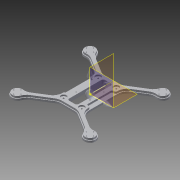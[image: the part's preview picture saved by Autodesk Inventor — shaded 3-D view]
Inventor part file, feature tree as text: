
AUTODESK INVENTOR PART (.ipt)
format: ipt  version: 2013 (Build 170138000, 138)  size: 2,560,512 bytes
history: native  units: mm
features: sketch x7, mirror x5, extrude x4, fillet x4, hole x4, projected_geometry x1
ambient origin geometry x8: Origin, YZ Plane, XZ Plane, XY Plane, X Axis, Y Axis, Z Axis, Center Point
feature tree (25):
  extrude  "Extrusion2"  Depth=80.0mm
  fillet  "Fillet1"  Radius=5.0mm
  fillet  "Fillet2"  Radius=5.0mm
  extrude  "Extrusion3"  Depth=30.0mm
  hole  "Hole1"  [1 undecoded]
  hole  "Hole2"  [1 undecoded]
  hole  "Hole3"  [1 undecoded]
  mirror  "Mirror1"
  mirror  "Mirror2"
  hole  "Hole4"  [1 undecoded]
  mirror  "Mirror3"
  mirror  "Mirror4"
  extrude  "Extrusion4"  Depth=20.0mm
  fillet  "Fillet3"  Radius=38.0mm
  extrude  "Extrusion5"  Depth=8.0mm
  mirror  "Mirror5"
  fillet  "Fillet5"  Radius=40.0mm
  sketch  "Sketch3"  dims[d13=80.0mm d14=80.0mm d15=5.0mm d16=5.0mm]
  sketch  "Sketch4"  dims[d17=25.0mm d18=30.0mm]
  sketch  "Sketch5"  dims[d19=49.0mm d20=4.0mm d21=0.0mm]
  sketch  "Sketch6"  dims[d22=20.0mm d23=20.0mm]
  sketch  "Sketch8"  dims[d24=7.0mm d26=4.0mm d27=0.0mm]
  sketch  "Sketch9"  dims[d28=30.5mm d30=30.5mm]
  projected_geometry  "Projected Loop2"
  sketch  "Sketch10"  dims[d31=2.1mm d32=6.0mm d33=4.0mm d34=2.0mm d35=90.0deg d36=8.0mm d37=20.594885mm d40=12.0mm d41=6.0mm d42=4.0mm d43=2.0mm d44=90.0deg d45=3.0mm d46=0.0mm d91=10.0mm d92=10.0mm d49=3.1mm d50=6.0mm d51=4.0mm d52=2.0mm d53=90.0deg d54=4.0mm d55=0.0mm d58=20.0mm d59=38.0mm d60=8.0mm d61=40.0mm d63=360.0deg d65=2.1mm d66=6.0mm d67=4.0mm d68=2.0mm d69=90.0deg d70=8.0mm d71=20.594885mm d72=8.0mm d73=8.0mm d74=18.0mm d75=18.0mm d76=11.5mm d77=0.0mm d78=4.0mm d84=10.0mm d85=10.0mm d86=10.0mm d87=4.0mm d88=0.0mm d90=3.0mm]
note: 4 required parameter values undecoded (feature->parameter linkage not recoverable at this tier; creation-order binding heuristic only, values carry confidence <= 0.55)
